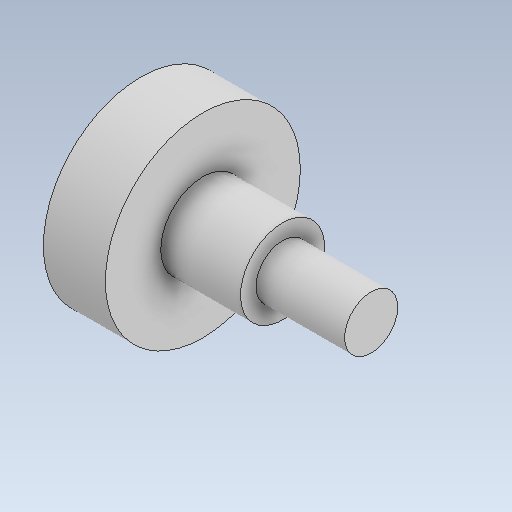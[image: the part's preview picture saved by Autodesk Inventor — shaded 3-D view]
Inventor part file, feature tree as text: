
AUTODESK INVENTOR PART (.ipt)
format: ipt  version: 2020 (Build 240168000, 168)  size: 118,272 bytes
history: native  units: mm
features: other x3, sketch x1
ambient origin geometry x8: Origin, YZ Plane, XZ Plane, XY Plane, X Axis, Y Axis, Z Axis, Center Point
bodies: Solid1 (feature_tree)
feature tree (4):
  other  "guia.ipt"
  other  "Solid1::guia.ipt"
  other  "TaggingFeature1"
  sketch  "Sketch1"  dims[d0=10.0mm]
